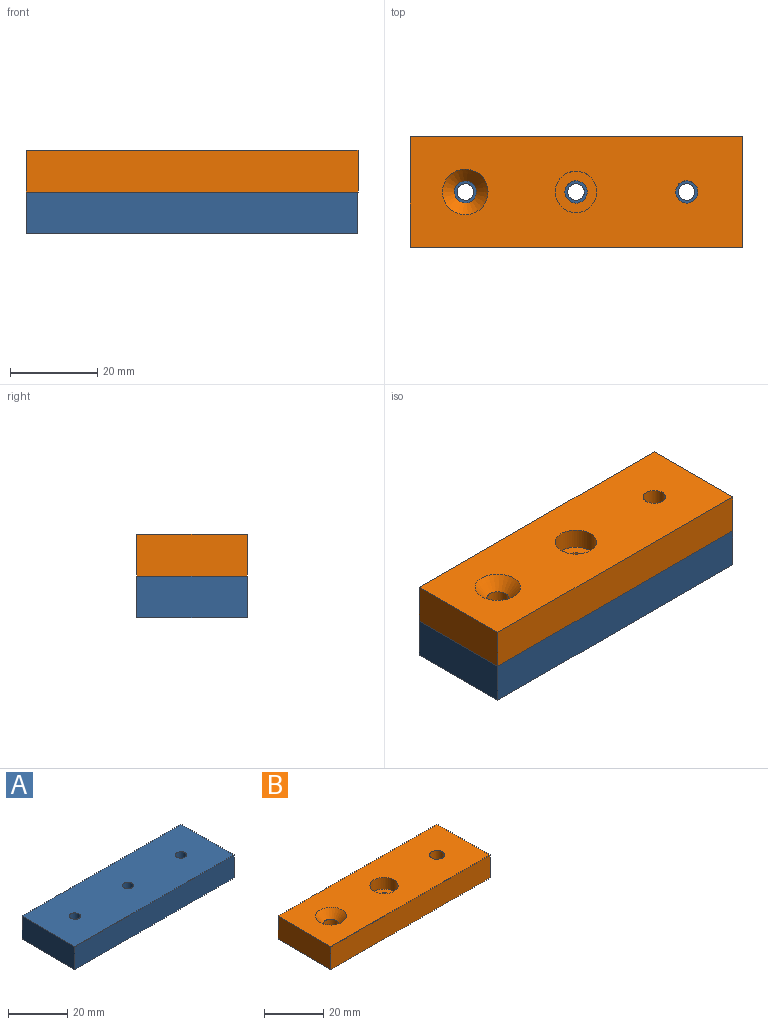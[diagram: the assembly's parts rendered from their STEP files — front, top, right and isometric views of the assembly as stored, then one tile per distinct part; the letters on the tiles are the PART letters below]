
ASSEMBLY  parts=2 mates=1
PART A: 9 faces, bbox 76.2x25.4x9.5 mm
  f0: plane 25.4x9.53mm, normal (-1,0,0), area 241.9mm2, adj f1,f3,f4,f5
  f1: plane 76.2x9.53mm, normal (0,-1,0), area 725.8mm2, adj f0,f2,f4,f5
  f2: plane 25.4x9.53mm, normal (1,0,0), area 241.9mm2, adj f1,f3,f4,f5
  f3: plane 76.2x9.53mm, normal (0,1,0), area 725.8mm2, adj f0,f2,f4,f5
  f4: plane 76.2x25.4mm, normal (0,0,-1), area 1901.5mm2, adj f0,f1,f2,f3,f6,f7,f8
  f5: plane 76.2x25.4mm, normal (0,0,1), area 1901.5mm2, adj f0,f1,f2,f3,f6,f7,f8
  f6: cylinder r=1.9mm len=9.53mm, axis (0,0,1), area 113.6mm2, adj f4,f5
  f7: cylinder r=1.9mm len=9.53mm, axis (0,0,1), area 113.6mm2, adj f4,f5
  f8: cylinder r=1.9mm len=9.53mm, axis (0,0,1), area 113.6mm2, adj f4,f5
PART B: 12 faces, bbox 76.2x25.4x9.5 mm
  f0: plane 25.4x9.53mm, normal (-1,0,0), area 241.9mm2, adj f1,f3,f4,f5
  f1: plane 76.2x9.53mm, normal (0,-1,0), area 725.8mm2, adj f0,f2,f4,f5
  f2: plane 25.4x9.53mm, normal (1,0,0), area 241.9mm2, adj f1,f3,f4,f5
  f3: plane 76.2x9.53mm, normal (0,1,0), area 725.8mm2, adj f0,f2,f4,f5
  f4: plane 76.2x25.4mm, normal (0,0,-1), area 1874.1mm2, adj f0,f1,f2,f3,f6,f9,f11
  f5: plane 76.2x25.4mm, normal (0,0,1), area 1758.2mm2, adj f0,f1,f2,f3,f8,f10,f11
  f6: cylinder r=2.55mm len=5.11mm, axis (0,0,1), area 75.4mm2, adj f4,f7
  f7: plane 9.53x9.53mm, normal (0,0,1), area 50.8mm2, adj f6,f8
  f8: cylinder r=4.76mm len=9.53mm, axis (0,0,1), area 144.4mm2, adj f5,f7
  f9: cylinder r=2.55mm len=6.46mm, axis (0,0,1), area 103.6mm2, adj f4,f10
  f10: cone r=2.55mm half-angle=41deg, axis (0,0,1), area 99.3mm2, adj f5,f9
  f11: cylinder r=2.55mm len=9.53mm, axis (0,0,1), area 152.8mm2, adj f4,f5
PLACE A t=(0,0,-9.52)mm
PLACE B at identity fixed
MATE fastened B.f6 <-> A.f8  axis (0,0,-1) through (0,0,-9.52)mm
